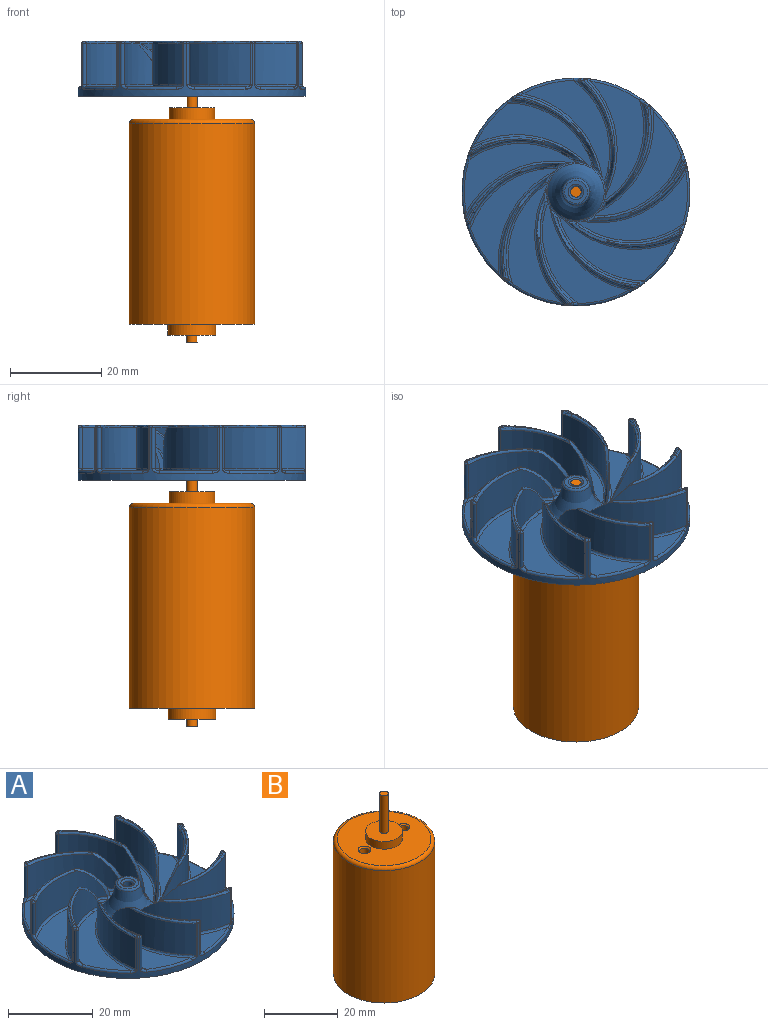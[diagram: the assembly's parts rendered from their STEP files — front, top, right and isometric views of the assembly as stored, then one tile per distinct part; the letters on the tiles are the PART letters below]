
ASSEMBLY  parts=2 mates=1
PART A: 188 faces, bbox 54.1x54.1x14 mm
  f0: plane 24.36x15.08mm, normal (0,0,1), area 126.6mm2, adj f172,f177,f181,f182
  f1: plane 22.96x19.16mm, normal (0,0,1), area 126.6mm2, adj f121,f169,f170,f177
  f2: plane 26.18x11.6mm, normal (0,0,1), area 126.6mm2, adj f118,f166,f167,f177
  f3: plane 22.34x19mm, normal (0,0,1), area 126.6mm2, adj f115,f163,f164,f177
  f4: plane 25.83x14.11mm, normal (0,0,1), area 126.6mm2, adj f112,f160,f161,f177
  f5: plane 24.36x15.08mm, normal (0,0,1), area 126.6mm2, adj f109,f157,f158,f177
  f6: plane 22.96x19.16mm, normal (0,0,1), area 126.6mm2, adj f106,f154,f155,f177
  f7: plane 26.18x11.6mm, normal (0,0,1), area 126.6mm2, adj f103,f151,f152,f177
  f8: plane 22.34x19mm, normal (0,0,1), area 126.6mm2, adj f100,f148,f149,f177
  f9: cylinder r=20mm len=17.71mm, axis (0,0,-1), area 193.9mm2, adj f52,f55,f98,f146
  f10: cylinder r=21.5mm len=17.8mm, axis (0,0,-1), area 204.3mm2, adj f52,f56,f99,f148
  f11: cylinder r=20mm len=21.95mm, axis (0,0,-1), area 193.9mm2, adj f51,f57,f101,f149
  f12: cylinder r=21.5mm len=23.57mm, axis (0,0,-1), area 204.3mm2, adj f51,f58,f102,f151
  f13: cylinder r=20mm len=21.26mm, axis (0,0,-1), area 193.9mm2, adj f50,f60,f104,f152
  f14: cylinder r=21.5mm len=21.93mm, axis (0,0,-1), area 204.3mm2, adj f50,f61,f105,f154
  f15: cylinder r=20mm len=19.04mm, axis (0,0,-1), area 193.9mm2, adj f49,f63,f107,f155
  f16: cylinder r=21.5mm len=20.91mm, axis (0,0,-1), area 204.3mm2, adj f49,f64,f108,f157
  f17: cylinder r=20mm len=22.72mm, axis (0,0,-1), area 193.9mm2, adj f48,f66,f110,f158
  f18: cylinder r=21.5mm len=23.92mm, axis (0,0,-1), area 204.3mm2, adj f48,f67,f111,f160
  f19: cylinder r=20mm len=17.71mm, axis (0,0,-1), area 193.9mm2, adj f47,f69,f113,f161
  f20: cylinder r=21.5mm len=17.8mm, axis (0,0,-1), area 204.3mm2, adj f47,f70,f114,f163
  f21: cylinder r=20mm len=21.95mm, axis (0,0,-1), area 193.9mm2, adj f46,f72,f116,f164
  f22: cylinder r=21.5mm len=23.57mm, axis (0,0,-1), area 204.3mm2, adj f46,f73,f117,f166
  f23: cylinder r=20mm len=21.26mm, axis (0,0,-1), area 193.9mm2, adj f45,f75,f119,f167
  f24: cylinder r=21.5mm len=21.93mm, axis (0,0,-1), area 204.3mm2, adj f45,f76,f120,f169
  f25: cylinder r=20mm len=19.04mm, axis (0,0,-1), area 193.9mm2, adj f44,f94,f122,f170
  f26: cylinder r=21.5mm len=20.91mm, axis (0,0,-1), area 204.3mm2, adj f44,f123,f172,f173
  f27: cylinder r=20mm len=22.72mm, axis (0,0,-1), area 193.9mm2, adj f43,f180,f181,f185
  f28: cylinder r=21.5mm len=23.92mm, axis (0,0,-1), area 204.3mm2, adj f43,f144,f145,f175
  f29: plane 25.83x14.11mm, normal (0,0,1), area 126.6mm2, adj f97,f145,f146,f177
  f30: cylinder r=1.18mm len=9.5mm, axis (0,0,-1), area 70.1mm2, adj f32,f186
  f31: cylinder r=25mm len=50mm, axis (0,0,-1), area 306.1mm2, adj f32,f59,f62,f65,f68,f71,f74,f77
  f32: plane 50x50mm, normal (0,0,-1), area 1959.2mm2, adj f30,f31
  f33: plane 8.38x2.82mm, normal (0,0,1), area 1.6mm2, adj f55,f56,f59
  f34: plane 6.93x5.32mm, normal (0,0,1), area 1.6mm2, adj f57,f58,f62
  f35: plane 8.73x0.78mm, normal (0,0,1), area 1.6mm2, adj f60,f61,f65
  f36: plane 7.2x5.11mm, normal (0,0,1), area 1.6mm2, adj f63,f64,f68
  f37: plane 8.23x2.92mm, normal (0,0,1), area 1.6mm2, adj f66,f67,f71
  f38: plane 8.38x2.82mm, normal (0,0,1), area 1.6mm2, adj f69,f70,f74
  f39: plane 6.93x5.32mm, normal (0,0,1), area 1.6mm2, adj f72,f73,f77
  f40: plane 8.73x0.78mm, normal (0,0,1), area 1.6mm2, adj f75,f76,f78
  f41: plane 7.2x5.11mm, normal (0,0,1), area 1.6mm2, adj f94,f123,f124
  f42: plane 8.23x2.92mm, normal (0,0,1), area 1.6mm2, adj f175,f179,f180
  f43: torus R=20mm, axis (0,0,-1), area 10.1mm2, adj f27,f28,f145,f175,f176,f180,f181
  f44: torus R=20mm, axis (0,0,-1), area 10.1mm2, adj f25,f26,f94,f123,f170,f171,f172
  f45: torus R=20mm, axis (0,0,-1), area 10.1mm2, adj f23,f24,f75,f76,f167,f168,f169
  f46: torus R=20mm, axis (0,0,-1), area 10.1mm2, adj f21,f22,f72,f73,f164,f165,f166
  f47: torus R=20mm, axis (0,0,-1), area 10.1mm2, adj f19,f20,f69,f70,f161,f162,f163
  f48: torus R=20mm, axis (0,0,-1), area 10.1mm2, adj f17,f18,f66,f67,f158,f159,f160
  f49: torus R=20mm, axis (0,0,-1), area 10.1mm2, adj f15,f16,f63,f64,f155,f156,f157
  f50: torus R=20mm, axis (0,0,-1), area 10.1mm2, adj f13,f14,f60,f61,f152,f153,f154
  f51: torus R=20mm, axis (0,0,-1), area 10.1mm2, adj f11,f12,f57,f58,f149,f150,f151
  f52: torus R=20mm, axis (0,0,-1), area 10.1mm2, adj f9,f10,f55,f56,f146,f147,f148
  f53: plane 5.02x5.02mm, normal (0,0,1), area 11mm2, adj f186,f187
  f54: torus R=14.23mm, axis (0,0,1), area 214.3mm2, adj f177,f187
  f55: torus R=20.5mm, axis (0,0,1), area 12.3mm2, adj f9,f33,f52,f56,f79
  f56: torus R=21mm, axis (0,0,1), area 12.6mm2, adj f10,f33,f52,f55,f80
  f57: torus R=20.5mm, axis (0,0,1), area 12.3mm2, adj f11,f34,f51,f58,f81
  f58: torus R=21mm, axis (0,0,1), area 12.6mm2, adj f12,f34,f51,f57,f82
  f59: torus R=24.5mm, axis (0,0,1), area 0.5mm2, adj f31,f33,f79,f80
  f60: torus R=20.5mm, axis (0,0,1), area 12.3mm2, adj f13,f35,f50,f61,f83
  f61: torus R=21mm, axis (0,0,1), area 12.6mm2, adj f14,f35,f50,f60,f84
  f62: torus R=24.5mm, axis (0,0,1), area 0.5mm2, adj f31,f34,f81,f82
  f63: torus R=20.5mm, axis (0,0,1), area 12.3mm2, adj f15,f36,f49,f64,f85
  f64: torus R=21mm, axis (0,0,1), area 12.6mm2, adj f16,f36,f49,f63,f86
  f65: torus R=24.5mm, axis (0,0,1), area 0.5mm2, adj f31,f35,f83,f84
  f66: torus R=20.5mm, axis (0,0,1), area 12.3mm2, adj f17,f37,f48,f67,f87
  f67: torus R=21mm, axis (0,0,1), area 12.6mm2, adj f18,f37,f48,f66,f88
  f68: torus R=24.5mm, axis (0,0,1), area 0.5mm2, adj f31,f36,f85,f86
  f69: torus R=20.5mm, axis (0,0,1), area 12.3mm2, adj f19,f38,f47,f70,f89
  f70: torus R=21mm, axis (0,0,1), area 12.6mm2, adj f20,f38,f47,f69,f90
  f71: torus R=24.5mm, axis (0,0,1), area 0.5mm2, adj f31,f37,f87,f88
  f72: torus R=20.5mm, axis (0,0,1), area 12.3mm2, adj f21,f39,f46,f73,f91
  f73: torus R=21mm, axis (0,0,1), area 12.6mm2, adj f22,f39,f46,f72,f92
  f74: torus R=24.5mm, axis (0,0,1), area 0.5mm2, adj f31,f38,f89,f90
  f75: torus R=20.5mm, axis (0,0,1), area 12.3mm2, adj f23,f40,f45,f76,f93
  f76: torus R=21mm, axis (0,0,1), area 12.6mm2, adj f24,f40,f45,f75,f95
  f77: torus R=24.5mm, axis (0,0,1), area 0.5mm2, adj f31,f39,f91,f92
  f78: torus R=24.5mm, axis (0,0,1), area 0.5mm2, adj f31,f40,f93,f95
  f79: sphere r=0.5mm, area 0.6mm2, adj f55,f59,f98
  f80: sphere r=0.5mm, area 0.2mm2, adj f56,f59,f99
  f81: sphere r=0.5mm, area 0.6mm2, adj f57,f62,f101
  f82: sphere r=0.5mm, area 0.2mm2, adj f58,f62,f102
  f83: sphere r=0.5mm, area 0.6mm2, adj f60,f65,f104
  f84: sphere r=0.5mm, area 0.2mm2, adj f61,f65,f105
  f85: sphere r=0.5mm, area 0.6mm2, adj f63,f68,f107
  f86: sphere r=0.5mm, area 0.2mm2, adj f64,f68,f108
  f87: sphere r=0.5mm, area 0.6mm2, adj f66,f71,f110
  f88: sphere r=0.5mm, area 0.2mm2, adj f67,f71,f111
  f89: sphere r=0.5mm, area 0.6mm2, adj f69,f74,f113
  f90: sphere r=0.5mm, area 0.2mm2, adj f70,f74,f114
  f91: sphere r=0.5mm, area 0.6mm2, adj f72,f77,f116
  f92: sphere r=0.5mm, area 0.2mm2, adj f73,f77,f117
  f93: sphere r=0.5mm, area 0.6mm2, adj f75,f78,f119
  f94: torus R=20.5mm, axis (0,0,1), area 12.3mm2, adj f25,f41,f44,f96,f123
  f95: sphere r=0.5mm, area 0.2mm2, adj f76,f78,f120
  f96: sphere r=0.5mm, area 0.6mm2, adj f94,f122,f124
  f97: torus R=24.5mm, axis (0,0,1), area 9.2mm2, adj f29,f31,f125,f126
  f98: cylinder r=0.5mm len=9mm, axis (0,0,1), area 11.2mm2, adj f9,f31,f79,f126
  f99: cylinder r=0.5mm len=9mm, axis (0,0,-1), area 3.2mm2, adj f10,f31,f80,f127
  f100: torus R=24.5mm, axis (0,0,1), area 9.2mm2, adj f8,f31,f127,f128
  f101: cylinder r=0.5mm len=9mm, axis (0,0,1), area 11.2mm2, adj f11,f31,f81,f128
  f102: cylinder r=0.5mm len=9mm, axis (0,0,-1), area 3.2mm2, adj f12,f31,f82,f129
  f103: torus R=24.5mm, axis (0,0,1), area 9.2mm2, adj f7,f31,f129,f130
  f104: cylinder r=0.5mm len=9mm, axis (0,0,1), area 11.2mm2, adj f13,f31,f83,f130
  f105: cylinder r=0.5mm len=9mm, axis (0,0,-1), area 3.2mm2, adj f14,f31,f84,f131
  f106: torus R=24.5mm, axis (0,0,1), area 9.2mm2, adj f6,f31,f131,f132
  f107: cylinder r=0.5mm len=9mm, axis (0,0,1), area 11.2mm2, adj f15,f31,f85,f132
  f108: cylinder r=0.5mm len=9mm, axis (0,0,-1), area 3.2mm2, adj f16,f31,f86,f133
  f109: torus R=24.5mm, axis (0,0,1), area 9.2mm2, adj f5,f31,f133,f134
  f110: cylinder r=0.5mm len=9mm, axis (0,0,1), area 11.2mm2, adj f17,f31,f87,f134
  f111: cylinder r=0.5mm len=9mm, axis (0,0,-1), area 3.2mm2, adj f18,f31,f88,f135
  f112: torus R=24.5mm, axis (0,0,1), area 9.2mm2, adj f4,f31,f135,f136
  f113: cylinder r=0.5mm len=9mm, axis (0,0,1), area 11.2mm2, adj f19,f31,f89,f136
  f114: cylinder r=0.5mm len=9mm, axis (0,0,-1), area 3.2mm2, adj f20,f31,f90,f137
  f115: torus R=24.5mm, axis (0,0,1), area 9.2mm2, adj f3,f31,f137,f138
  f116: cylinder r=0.5mm len=9mm, axis (0,0,1), area 11.2mm2, adj f21,f31,f91,f138
  f117: cylinder r=0.5mm len=9mm, axis (0,0,-1), area 3.2mm2, adj f22,f31,f92,f139
  f118: torus R=24.5mm, axis (0,0,1), area 9.2mm2, adj f2,f31,f139,f140
  f119: cylinder r=0.5mm len=9mm, axis (0,0,1), area 11.2mm2, adj f23,f31,f93,f140
  f120: cylinder r=0.5mm len=9mm, axis (0,0,-1), area 3.2mm2, adj f24,f31,f95,f141
  f121: torus R=24.5mm, axis (0,0,1), area 9.2mm2, adj f1,f31,f141,f142
  f122: cylinder r=0.5mm len=9mm, axis (0,0,1), area 11.2mm2, adj f25,f31,f96,f142
  f123: torus R=21mm, axis (0,0,1), area 12.6mm2, adj f26,f41,f44,f94,f143
  f124: torus R=24.5mm, axis (0,0,1), area 0.5mm2, adj f31,f41,f96,f143
  f125: bspline ~1.64x1.21mm, area 0.9mm2, adj f31,f97,f144,f145
  f126: bspline ~1.65x1.38mm, area 1.6mm2, adj f31,f97,f98,f146
  f127: bspline ~1.77x1.17mm, area 0.9mm2, adj f31,f99,f100,f148
  f128: bspline ~1.74x1.34mm, area 1.6mm2, adj f31,f100,f101,f149
  f129: bspline ~1.78x1.17mm, area 0.9mm2, adj f31,f102,f103,f151
  f130: bspline ~1.66x1.54mm, area 1.6mm2, adj f31,f103,f104,f152
  f131: bspline ~1.57x1.33mm, area 0.9mm2, adj f31,f105,f106,f154
  f132: bspline ~2.11x1.34mm, area 1.6mm2, adj f31,f106,f107,f155
  f133: bspline ~1.81x1.17mm, area 0.9mm2, adj f31,f108,f109,f157
  f134: bspline ~1.77x1.34mm, area 1.6mm2, adj f31,f109,f110,f158
  f135: bspline ~1.64x1.21mm, area 0.9mm2, adj f31,f111,f112,f160
  f136: bspline ~1.65x1.38mm, area 1.6mm2, adj f31,f112,f113,f161
  f137: bspline ~1.77x1.17mm, area 0.9mm2, adj f31,f114,f115,f163
  f138: bspline ~1.74x1.34mm, area 1.6mm2, adj f31,f115,f116,f164
  f139: bspline ~1.78x1.17mm, area 0.9mm2, adj f31,f117,f118,f166
  f140: bspline ~1.66x1.54mm, area 1.6mm2, adj f31,f118,f119,f167
  f141: bspline ~1.57x1.33mm, area 0.9mm2, adj f31,f120,f121,f169
  f142: bspline ~2.11x1.34mm, area 1.6mm2, adj f31,f121,f122,f170
  f143: sphere r=0.5mm, area 0.2mm2, adj f123,f124,f173
  f144: cylinder r=0.5mm len=9mm, axis (0,0,-1), area 3.2mm2, adj f28,f31,f125,f174
  f145: torus R=22mm, axis (0,0,1), area 20.4mm2, adj f28,f29,f43,f125,f176,f177
  f146: torus R=19.5mm, axis (0,0,1), area 19.2mm2, adj f9,f29,f52,f126,f147,f177
  f147: torus R=6.55mm, axis (0,0,-1), area 1.3mm2, adj f52,f146,f148,f177
  f148: torus R=22mm, axis (0,0,1), area 20.4mm2, adj f8,f10,f52,f127,f147,f177
  f149: torus R=19.5mm, axis (0,0,1), area 19.2mm2, adj f8,f11,f51,f128,f150,f177
  f150: torus R=6.55mm, axis (0,0,-1), area 1.3mm2, adj f51,f149,f151,f177
  f151: torus R=22mm, axis (0,0,1), area 20.4mm2, adj f7,f12,f51,f129,f150,f177
  f152: torus R=19.5mm, axis (0,0,1), area 19.2mm2, adj f7,f13,f50,f130,f153,f177
  f153: torus R=6.55mm, axis (0,0,-1), area 1.3mm2, adj f50,f152,f154,f177
  f154: torus R=22mm, axis (0,0,1), area 20.4mm2, adj f6,f14,f50,f131,f153,f177
  f155: torus R=19.5mm, axis (0,0,1), area 19.2mm2, adj f6,f15,f49,f132,f156,f177
  f156: torus R=6.55mm, axis (0,0,-1), area 1.3mm2, adj f49,f155,f157,f177
  f157: torus R=22mm, axis (0,0,1), area 20.4mm2, adj f5,f16,f49,f133,f156,f177
  f158: torus R=19.5mm, axis (0,0,1), area 19.2mm2, adj f5,f17,f48,f134,f159,f177
  f159: torus R=6.55mm, axis (0,0,-1), area 1.3mm2, adj f48,f158,f160,f177
  f160: torus R=22mm, axis (0,0,1), area 20.4mm2, adj f4,f18,f48,f135,f159,f177
  f161: torus R=19.5mm, axis (0,0,1), area 19.2mm2, adj f4,f19,f47,f136,f162,f177
  f162: torus R=6.55mm, axis (0,0,-1), area 1.3mm2, adj f47,f161,f163,f177
  f163: torus R=22mm, axis (0,0,1), area 20.4mm2, adj f3,f20,f47,f137,f162,f177
  f164: torus R=19.5mm, axis (0,0,1), area 19.2mm2, adj f3,f21,f46,f138,f165,f177
  f165: torus R=6.55mm, axis (0,0,-1), area 1.3mm2, adj f46,f164,f166,f177
  f166: torus R=22mm, axis (0,0,1), area 20.4mm2, adj f2,f22,f46,f139,f165,f177
  f167: torus R=19.5mm, axis (0,0,1), area 19.2mm2, adj f2,f23,f45,f140,f168,f177
  f168: torus R=6.55mm, axis (0,0,-1), area 1.3mm2, adj f45,f167,f169,f177
  f169: torus R=22mm, axis (0,0,1), area 20.4mm2, adj f1,f24,f45,f141,f168,f177
  f170: torus R=19.5mm, axis (0,0,1), area 19.2mm2, adj f1,f25,f44,f142,f171,f177
  f171: torus R=6.55mm, axis (0,0,-1), area 1.3mm2, adj f44,f170,f172,f177
  f172: torus R=22mm, axis (0,0,1), area 20.4mm2, adj f0,f26,f44,f171,f177,f178
  f173: cylinder r=0.5mm len=9mm, axis (0,0,-1), area 3.2mm2, adj f26,f31,f143,f178
  f174: sphere r=0.5mm, area 0.2mm2, adj f144,f175,f179
  f175: torus R=21mm, axis (0,0,1), area 12.6mm2, adj f28,f42,f43,f174,f180
  f176: torus R=6.55mm, axis (0,0,-1), area 1.3mm2, adj f43,f145,f177,f181
  f177: torus R=6.56mm, axis (0,0,-1), area 15.8mm2, adj f0,f1,f2,f3,f4,f5,f6,f7
  f178: bspline ~1.81x1.17mm, area 0.9mm2, adj f31,f172,f173,f182
  f179: torus R=24.5mm, axis (0,0,1), area 0.5mm2, adj f31,f42,f174,f183
  f180: torus R=20.5mm, axis (0,0,1), area 12.3mm2, adj f27,f42,f43,f175,f183
  f181: torus R=19.5mm, axis (0,0,1), area 19.2mm2, adj f0,f27,f43,f176,f177,f184
  f182: torus R=24.5mm, axis (0,0,1), area 9.2mm2, adj f0,f31,f178,f184
  f183: sphere r=0.5mm, area 0.6mm2, adj f179,f180,f185
  f184: bspline ~1.77x1.34mm, area 1.6mm2, adj f31,f181,f182,f185
  f185: cylinder r=0.5mm len=9mm, axis (0,0,1), area 11.2mm2, adj f27,f31,f183,f184
  f186: torus R=1.68mm, axis (0,0,1), area 6.7mm2, adj f30,f53
  f187: torus R=2.51mm, axis (0,0,-1), area 13.6mm2, adj f53,f54
PART B: 18 faces, bbox 29.8x29.8x64 mm
  f0: cylinder r=13.75mm len=44mm, axis (0,0,-1), area 3801.3mm2, adj f2,f5
  f1: plane 25.5x25.5mm, normal (0,0,1), area 412.9mm2, adj f5,f6,f13,f16
  f2: plane 27.5x27.5mm, normal (0,0,-1), area 507.4mm2, adj f0,f3
  f3: cylinder r=5.25mm len=10.5mm, axis (0,0,1), area 79.2mm2, adj f2,f4
  f4: plane 10.5x10.5mm, normal (0,0,-1), area 82.4mm2, adj f3,f10
  f5: torus R=12.75mm, axis (0,0,1), area 132.1mm2, adj f0,f1
  f6: cylinder r=5mm len=10mm, axis (0,0,-1), area 78.5mm2, adj f1,f7
  f7: plane 10x10mm, normal (0,0,1), area 74.4mm2, adj f6,f9
  f8: plane 2.3x2.3mm, normal (0,0,1), area 4.2mm2, adj f9
  f9: cylinder r=1.15mm len=12.5mm, axis (0,0,-1), area 90.3mm2, adj f7,f8
  f10: cylinder r=1.15mm len=2.3mm, axis (0,0,-1), area 11.6mm2, adj f4,f11
  f11: plane 2.3x2.3mm, normal (0,0,-1), area 4.2mm2, adj f10
  f12: cylinder r=1.32mm len=2.65mm, axis (0,0,1), area 21.4mm2, adj f13,f14
  f13: cone r=1.32mm half-angle=45deg, axis (0,0,1), area 5.8mm2, adj f1,f12
  f14: cone r=0mm half-angle=59deg, axis (0,0,1), area 6.4mm2, adj f12
  f15: cylinder r=1.32mm len=2.65mm, axis (0,0,1), area 21.4mm2, adj f16,f17
  f16: cone r=1.32mm half-angle=45deg, axis (0,0,1), area 5.8mm2, adj f1,f15
  f17: cone r=0mm half-angle=59deg, axis (0,0,1), area 6.4mm2, adj f15
PLACE A t=(-24.03,39.46,2.72)mm
PLACE B t=(-24.03,39.46,-47.39)mm
MATE cylindrical A.f30 <-> B.f9  axis (0,0,1) through (-24.03,39.46,12.72)mm
